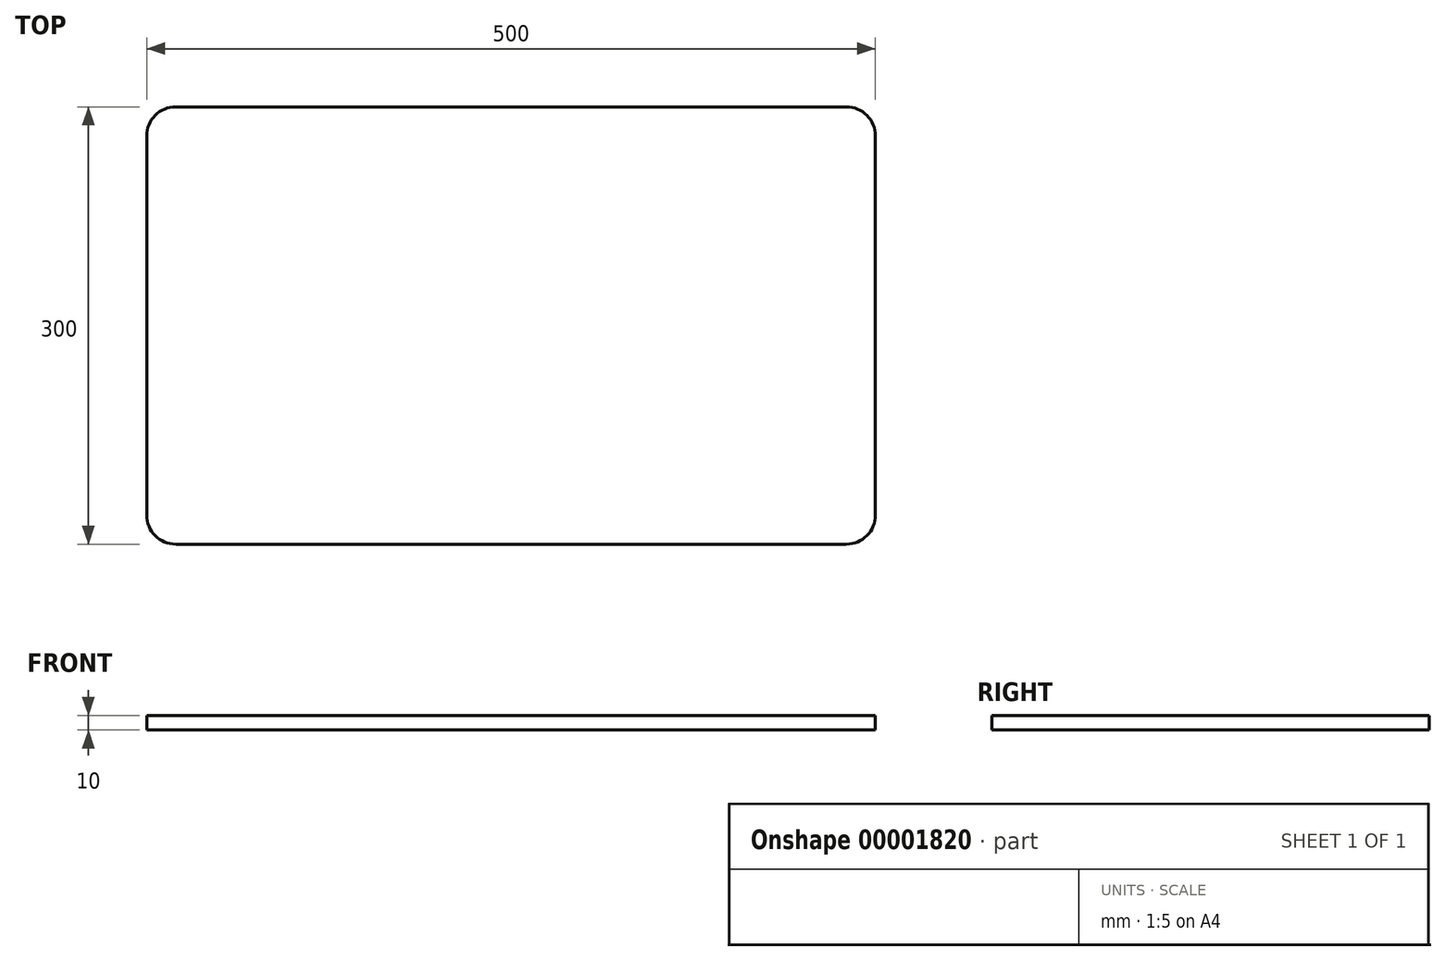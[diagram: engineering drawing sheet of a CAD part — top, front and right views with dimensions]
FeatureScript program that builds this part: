
annotation { "Feature Type Name" : "Feature", "Feature Type Description" : "" }
export const myFeature = defineFeature(function(context is Context, id is Id, definition is map)
    precondition{}
    {
        {
            var Q0;
            Q0=qCreatedBy(makeId("Top.planeOp"),FACE);
            var sketch = newSketch(context, id + "F0", { "sketchPlane" : qUnion([Q0])});
            skLineSegment(sketch, "E0.bottom", {"start": v(-197.52, 147.66) * mm, "end": v(302.48, 147.66) * mm});
            skLineSegment(sketch, "E0.top", {"start": v(-197.52, -152.34) * mm, "end": v(302.48, -152.34) * mm});
            skLineSegment(sketch, "E0.left", {"start": v(-197.52, 147.66) * mm, "end": v(-197.52, -152.34) * mm});
            skLineSegment(sketch, "E0.right", {"start": v(302.48, 147.66) * mm, "end": v(302.48, -152.34) * mm});
            skSolve(sketch);
        }
        {
            var Q0;
            Q0 = qSketchRegion(id + "F0", true);
            extrude(context, id + "F1", {"entities" : qUnion([Q0]), "depth" : 10 * mm});
        }
        {
            var Q0;
            Q0=makeQuery(id+"F1.opExtrude","SWEPT_FACE",FACE,{"disambiguationData":[OSD([sQuery(id+"F0.wireOp",EDGE,"E0.top")])]});
            var sketch = newSketch(context, id + "F2", { "sketchPlane" : qUnion([Q0])});
            skLineSegment(sketch, "E1", {"start": v(52.48, 10) * mm, "end": v(52.48, 0) * mm, "construction": true});
            skLineSegment(sketch, "E2", {"start": v(52.48, 0) * mm, "end": v(140.93, 0) * mm, "construction": true});
            skLineSegment(sketch, "E3", {"start": v(140.93, 0) * mm, "end": v(140.93, 10) * mm});
            skLineSegment(sketch, "E4", {"start": v(52.48, 0) * mm, "end": v(-35.97, 0) * mm, "construction": true});
            skLineSegment(sketch, "E5", {"start": v(-35.97, 0) * mm, "end": v(-35.97, 10) * mm});
            skSolve(sketch);
        }
        {
            var Q0;
            Q0=makeQuery(id+"F1.opExtrude","SWEPT_EDGE",EDGE,{"disambiguationData":[OSD([sQuery(id+"F0.wireOp",EDGE,"E0.top"),sQuery(id+"F0.wireOp",EDGE,"E0.left")])]});
            var Q1;
            Q1=makeQuery(id+"F1.opExtrude","SWEPT_EDGE",EDGE,{"disambiguationData":[OSD([sQuery(id+"F0.wireOp",EDGE,"E0.top"),sQuery(id+"F0.wireOp",EDGE,"E0.right")])]});
            var Q2;
            Q2=makeQuery(id+"F1.opExtrude","SWEPT_EDGE",EDGE,{"disambiguationData":[OSD([sQuery(id+"F0.wireOp",EDGE,"E0.bottom"),sQuery(id+"F0.wireOp",EDGE,"E0.right")])]});
            var Q3;
            Q3=makeQuery(id+"F1.opExtrude","SWEPT_EDGE",EDGE,{"disambiguationData":[OSD([sQuery(id+"F0.wireOp",EDGE,"E0.bottom"),sQuery(id+"F0.wireOp",EDGE,"E0.left")])]});
            fillet(context, id + "F3", {"entities" : qUnion([Q0, Q1, Q2, Q3]), "radius" : 20 * mm, "tangentPropagation" : true, "allowEdgeOverflow" : false});
        }
    });
